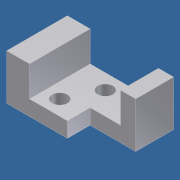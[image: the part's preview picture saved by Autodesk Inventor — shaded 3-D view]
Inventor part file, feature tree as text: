
AUTODESK INVENTOR PART (.ipt)
format: ipt  version: unknown  size: 198,656 bytes
history: native  units: in
note: dims shown in document units (in); Inventor stores cm internally (conversion verified against a paired STEP export)
features: sketch x4, extrude x3, hole x1
ambient origin geometry x8: Origin, YZ Plane, XZ Plane, XY Plane, X Axis, Y Axis, Z Axis, Center Point
bodies: Solid1 (feature_tree)
feature tree (8):
  extrude  "Extrusion1"  Depth=3.0in
  extrude  "Extrusion2"  Depth=1.5in
  extrude  "Extrusion3"  Depth=1.0in
  hole  "Hole1"  [1 undecoded]
  sketch  "Sketch1"  dims[d0=7.0in d1=3.0in]
  sketch  "Sketch2"  dims[d2=4.0in d3=0.0in d4=1.5in]
  sketch  "Sketch3"  dims[d5=2.0in d6=1.0in]
  sketch  "Sketch4"  dims[d7=4.5in d8=4.0in d9=0.0in d10=1.5in d11=3.0in d12=1.5in d13=3.0in d14=0.0in d15=1.0in d16=1.0in d17=2.0in d18=1.0in d19=1.0in d20=0.75in d21=0.375in d22=0.25in d23=0.5635in d24=1.0in d25=0.0in]
note: 1 required parameter value undecoded (feature->parameter linkage not recoverable at this tier; creation-order binding heuristic only, values carry confidence <= 0.55)
